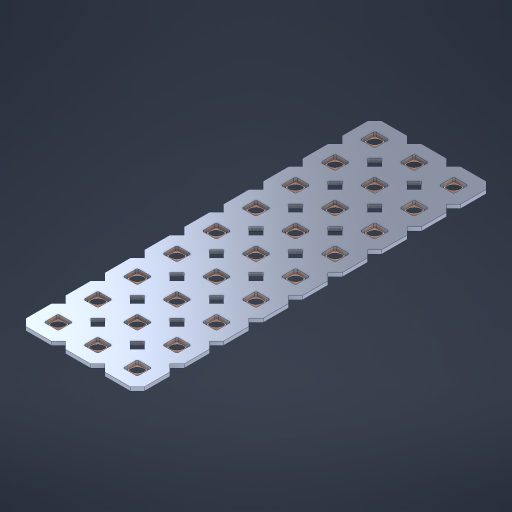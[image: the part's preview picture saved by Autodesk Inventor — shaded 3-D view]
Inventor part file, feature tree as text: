
AUTODESK INVENTOR PART (.ipt)
format: ipt  version: 2023 (Build 270158000, 158)  size: 565,248 bytes
history: native  units: in
note: dims shown in document units (in); Inventor stores cm internally (conversion verified against a paired STEP export)
features: other x28, extrude x26, sketch x2, pattern_linear x1
ambient origin geometry x8: Origin, YZ Plane, XZ Plane, XY Plane, X Axis, Y Axis, Z Axis, Center Point
bodies: Solid1 (feature_tree), Body (feature_tree)
feature tree (57):
  pattern_linear  "Rectangular Pattern1"  Spacing1=0.09in  [1 undecoded]
  sketch  "Sketch1"  dims[d1=0.5in]
  sketch  "Sketch2"  dims[d2=0.182in d3=0.09in d4=0.09in d5=0.09in d6=0.09in d7=0.09in d8=0.09in d9=0.09in d10=0.09in d11=0.02in d13=0.0in d14=0.172in d15=0.0625in d16=0.0in d19=0.5in d22=0.5in]
  other  "Srf1"
  other  "Srf126"
  other  "Srf127"
  other  "Srf128"
  other  "Srf129"
  other  "Srf130"
  other  "Srf131"
  other  "Srf250"
  other  "Srf251"
  other  "Srf268"
  other  "Srf269"
  other  "Srf270"
  other  "Srf271"
  other  "Srf272"
  other  "Srf273"
  other  "Srf274"
  other  "Srf275"
  other  "Srf276"
  other  "Srf293"
  other  "Srf294"
  other  "Srf295"
  other  "Srf296"
  other  "Srf297"
  other  "Srf298"
  other  "Srf299"
  other  "Srf300"
  other  "Srf301"
  other  "Circle"
  extrude  "ExtrusionSrf126"  Depth=0.09in
  extrude  "ExtrusionSrf127"  Depth=0.09in
  extrude  "ExtrusionSrf128"  Depth=0.09in
  extrude  "ExtrusionSrf129"  Depth=0.09in
  extrude  "ExtrusionSrf130"  Depth=0.09in
  extrude  "ExtrusionSrf131"  Depth=0.09in
  extrude  "ExtrusionSrf250"  Depth=0.09in
  extrude  "ExtrusionSrf251"  Depth=0.02in
  extrude  "ExtrusionSrf268"  TaperAngle=0.0deg  [1 undecoded]
  extrude  "ExtrusionSrf269"  Depth=0.5in
  extrude  "ExtrusionSrf270"  Depth=0.5in TaperAngle=0.0deg
  extrude  "ExtrusionSrf271"  Depth=0.5in
  extrude  "ExtrusionSrf272"  Depth=0.5in
  extrude  "ExtrusionSrf273"  [1 undecoded]
  extrude  "ExtrusionSrf274"  [1 undecoded]
  extrude  "ExtrusionSrf275"  [1 undecoded]
  extrude  "ExtrusionSrf276"  [1 undecoded]
  extrude  "ExtrusionSrf293"  [1 undecoded]
  extrude  "ExtrusionSrf294"  [1 undecoded]
  extrude  "ExtrusionSrf295"  [1 undecoded]
  extrude  "ExtrusionSrf296"  [1 undecoded]
  extrude  "ExtrusionSrf297"  [1 undecoded]
  extrude  "ExtrusionSrf298"  [1 undecoded]
  extrude  "ExtrusionSrf299"  [1 undecoded]
  extrude  "ExtrusionSrf300"  [1 undecoded]
  extrude  "ExtrusionSrf301"  [1 undecoded]
note: 15 required parameter values undecoded (feature->parameter linkage not recoverable at this tier; creation-order binding heuristic only, values carry confidence <= 0.55)
